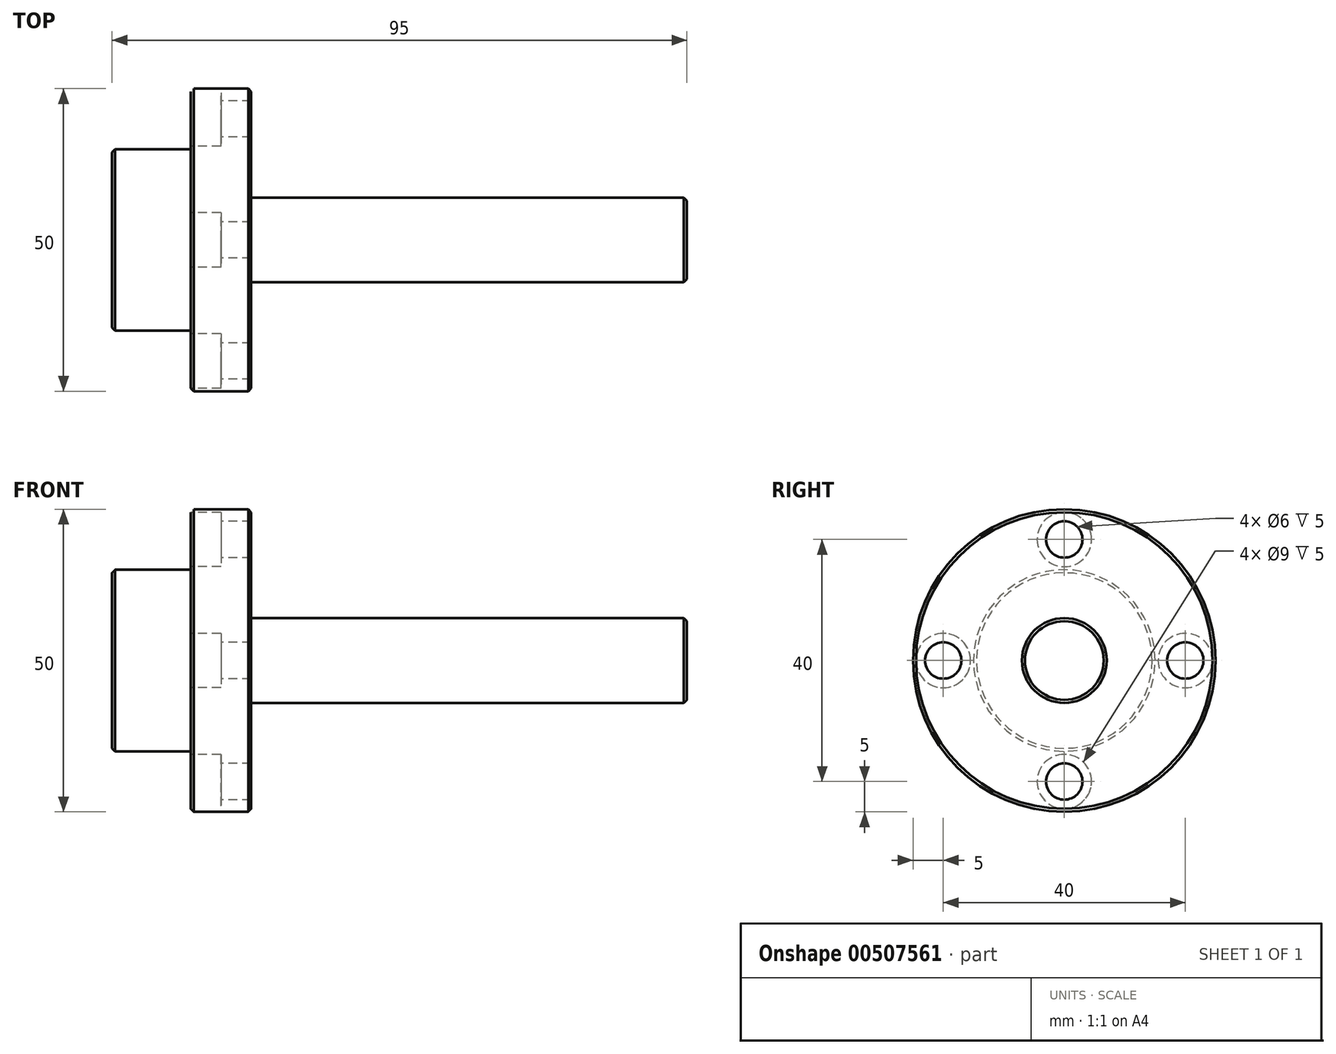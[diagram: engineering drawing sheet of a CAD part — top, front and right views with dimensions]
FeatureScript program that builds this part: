
annotation { "Feature Type Name" : "Feature", "Feature Type Description" : "" }
export const myFeature = defineFeature(function(context is Context, id is Id, definition is map)
    precondition{}
    {
        {
            var Q0;
            Q0=qCreatedBy(makeId("Front.planeOp"),FACE);
            var sketch = newSketch(context, id + "F0", { "sketchPlane" : qUnion([Q0])});
            skLineSegment(sketch, "E0", {"start": v(0, 0) * mm, "end": v(0, 15) * mm});
            skLineSegment(sketch, "E1", {"start": v(0, 15) * mm, "end": v(13, 15) * mm});
            skLineSegment(sketch, "E2", {"start": v(13, 15) * mm, "end": v(13, 25) * mm});
            skLineSegment(sketch, "E3", {"start": v(13, 25) * mm, "end": v(23, 25) * mm});
            skLineSegment(sketch, "E4", {"start": v(23, 25) * mm, "end": v(23, 7) * mm});
            skLineSegment(sketch, "E5", {"start": v(23, 7) * mm, "end": v(95, 7) * mm});
            skLineSegment(sketch, "E6", {"start": v(95, 7) * mm, "end": v(95, 0) * mm});
            skLineSegment(sketch, "E7", {"start": v(0, 0) * mm, "end": v(95, 0) * mm});
            skSolve(sketch);
        }
        {
            var Q0;
            Q0=makeQuery(id+"F0.imprint","IMPRINT",FACE,{"disambiguationData":[TD([[makeQuery(id+"F0.imprint","IMPRINT",EDGE,{"derivedFrom":sQuery(id+"F0.wireOp",EDGE,"E0")}),-1.0]])]});
            var Q1;
            Q1=sQuery(id+"F0.wireOp",EDGE,"E7");
            revolve(context, id + "F1", {"entities" : qUnion([Q0]), "axis" : qUnion([Q1]), "revolveType" : RevolveType.FULL});
        }
        {
            var Q0;
            Q0=makeQuery(id+"F1.opRevolve","SWEPT_FACE",FACE,{"disambiguationData":[OSD([sQuery(id+"F0.wireOp",EDGE,"E2")])]});
            var sketch = newSketch(context, id + "F2", { "sketchPlane" : qUnion([Q0])});
            skCircle(sketch, "E8", {"center": v(-20, 0) * mm, "radius": 3 * mm});
            skCircle(sketch, "E9.1.0", {"center": v(0, -20) * mm, "radius": 3 * mm});
            skCircle(sketch, "E9.2.0", {"center": v(20, 0) * mm, "radius": 3 * mm});
            skPoint(sketch, "E9.center", {"position": v(0, 0) * mm});
            skCircle(sketch, "E10.1.3.0", {"center": v(0, 20) * mm, "radius": 3 * mm});
            skSolve(sketch);
        }
        {
            var Q0;
            Q0=qSketchRegion(id+"F2",true);
            extrude(context, id + "F3", {"entities" : qUnion([Q0]), "operationType" : NewBodyOperationType.REMOVE, "oppositeDirection" : true, "depth" : 25 * mm});
        }
        {
            var Q0;
            Q0=makeQuery(id+"F1.opRevolve","SWEPT_FACE",FACE,{"disambiguationData":[OSD([sQuery(id+"F0.wireOp",EDGE,"E2")])]});
            var sketch = newSketch(context, id + "F4", { "sketchPlane" : qUnion([Q0])});
            skCircle(sketch, "E11", {"center": v(0, -20) * mm, "radius": 4.5 * mm});
            skCircle(sketch, "E12.1.0", {"center": v(20, 0) * mm, "radius": 4.5 * mm});
            skCircle(sketch, "E12.2.0", {"center": v(0, 20) * mm, "radius": 4.5 * mm});
            skCircle(sketch, "E12.3.0", {"center": v(-20, 0) * mm, "radius": 4.5 * mm});
            skPoint(sketch, "E12.center", {"position": v(0, 0) * mm});
            skSolve(sketch);
        }
        {
            var Q0;
            Q0=qSketchRegion(id+"F4",true);
            extrude(context, id + "F5", {"entities" : qUnion([Q0]), "operationType" : NewBodyOperationType.REMOVE, "oppositeDirection" : true, "depth" : 5 * mm});
        }
        {
            var Q0;
            Q0=makeQuery(id+"F1.opRevolve","SWEPT_EDGE",EDGE,{"disambiguationData":[OSD([sQuery(id+"F0.wireOp",EDGE,"E2"),sQuery(id+"F0.wireOp",EDGE,"E3")])]});
            var Q1;
            Q1=makeQuery(id+"F1.opRevolve","SWEPT_FACE",FACE,{"disambiguationData":[OSD([sQuery(id+"F0.wireOp",EDGE,"E0")])]});
            var Q2;
            Q2=makeQuery(id+"F1.opRevolve","SWEPT_EDGE",EDGE,{"disambiguationData":[OSD([sQuery(id+"F0.wireOp",EDGE,"E3"),sQuery(id+"F0.wireOp",EDGE,"E4")])]});
            var Q3;
            Q3=makeQuery(id+"F1.opRevolve","SWEPT_EDGE",EDGE,{"disambiguationData":[OSD([sQuery(id+"F0.wireOp",EDGE,"E5"),sQuery(id+"F0.wireOp",EDGE,"E6")])]});
            chamfer(context, id + "F6", {"entities" : qUnion([Q0, Q1, Q2, Q3]), "width" : 0.5 * mm, "tangentPropagation" : true});
        }
    });
